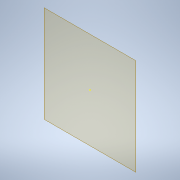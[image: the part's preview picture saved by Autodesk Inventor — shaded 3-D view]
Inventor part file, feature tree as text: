
AUTODESK INVENTOR PART (.ipt)
format: ipt  version: 2020 (Build 240168000, 168)  size: 82,432 bytes
history: native  units: in
note: dims shown in document units (in); Inventor stores cm internally (conversion verified against a paired STEP export)
features: other x3, plane x1, sketch x1
ambient origin geometry x8: Origin, YZ Plane, XZ Plane, XY Plane, X Axis, Y Axis, Z Axis, Center Point
feature tree (5):
  plane  "Work Plane1"
  sketch  "Sketch1"
  other  "<userpath>\Documents\inventor\md\Project\Assembly2.iam"
  other  "Assembly2.iam"
  other  "Part6:2"
